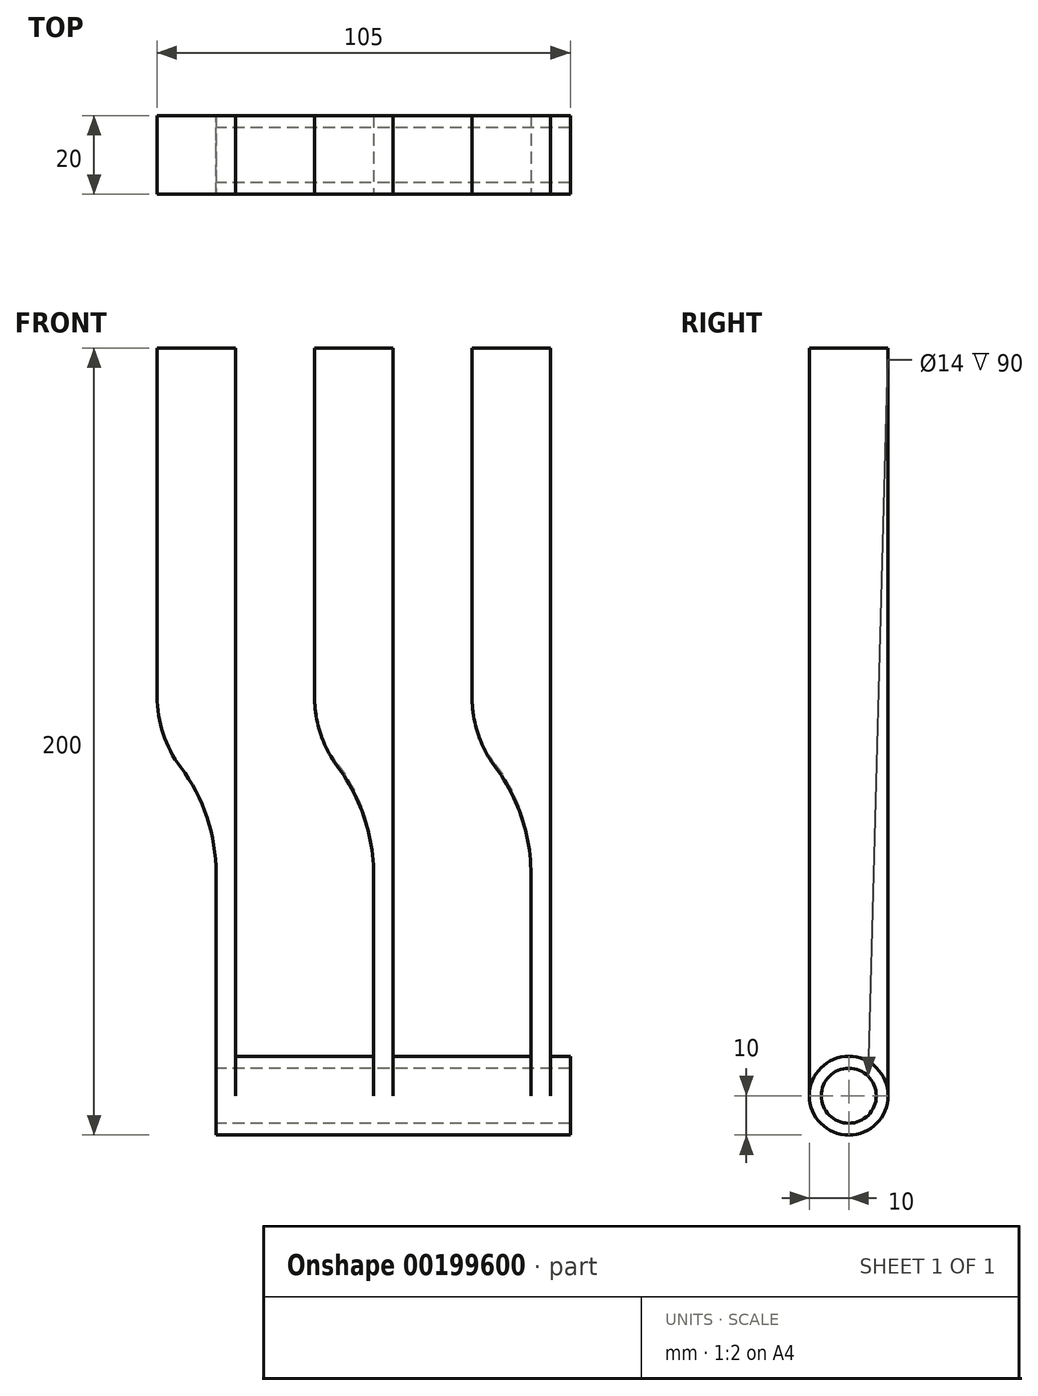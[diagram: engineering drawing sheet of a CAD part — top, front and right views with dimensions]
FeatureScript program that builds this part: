
annotation { "Feature Type Name" : "Feature", "Feature Type Description" : "" }
export const myFeature = defineFeature(function(context is Context, id is Id, definition is map)
    precondition{}
    {
        {
            assignVariable(context, id + "F0", {"name" : "width", "anyValue" : 120 * mm});
        }
        {
            var Q0;
            Q0=qCreatedBy(makeId("Front.planeOp"),FACE);
            var sketch = newSketch(context, id + "F1", { "sketchPlane" : qUnion([Q0])});
            skLineSegment(sketch, "E0.bottom", {"start": v(0, 0) * mm, "end": v(120, 0) * mm});
            skLineSegment(sketch, "E0.top", {"start": v(0, 200) * mm, "end": v(120, 200) * mm});
            skLineSegment(sketch, "E0.left", {"start": v(0, 0) * mm, "end": v(0, 200) * mm});
            skLineSegment(sketch, "E0.right", {"start": v(120, 0) * mm, "end": v(120, 200) * mm});
            skSolve(sketch);
        }
        {
            var Q0;
            Q0 = qSketchRegion(id + "F1", true);
            extrude(context, id + "F2", {"entities" : qUnion([Q0]), "depth" : 1 / 6 * getVariable(context, 'width')});
        }
        {
            var Q0;
            Q0=makeQuery(id+"F2.opExtrude","SWEPT_FACE",FACE,{"disambiguationData":[OSD([sQuery(id+"F1.wireOp",EDGE,"E0.left")])]});
            var sketch = newSketch(context, id + "F3", { "sketchPlane" : qUnion([Q0])});
            skCircle(sketch, "E1", {"center": v(10, 10) * mm, "radius": 10 * mm});
            skPoint(sketch, "E1.centerSnap0", {"position": v(10, 0) * mm});
            skSolve(sketch);
        }
        {
            var Q0;
            {var subQ0=sQuery(id+"F3.wireOp",EDGE,"E1");var subQ1=sQuery(id+"F1.wireOp",EDGE,"E0.left");var subQ2=makeQuery(id+"F2.opExtrude","CAP_EDGE",EDGE,{"disambiguationData":[OSD([subQ1])],"isStart":false});var subQ3=makeQuery(id+"F3.imprint","INTERSECT",VERTEX,{"derivedFrom":[subQ2,subQ0]});Q0=makeQuery(id+"F3.imprint","IMPRINT",FACE,{"disambiguationData":[TD([[makeQuery(id+"F3.imprint","IMPRINT",EDGE,{"disambiguationData":[TD([[subQ3,1.0]])],"derivedFrom":subQ0}),-1.0]])]});}
            var Q1;
            {var subQ0=sQuery(id+"F3.wireOp",EDGE,"E1");var subQ1=sQuery(id+"F1.wireOp",EDGE,"E0.left");var subQ2=makeQuery(id+"F2.opExtrude","CAP_EDGE",EDGE,{"disambiguationData":[OSD([subQ1])],"isStart":true});var subQ3=makeQuery(id+"F3.imprint","INTERSECT",VERTEX,{"derivedFrom":[subQ2,subQ0]});Q1=makeQuery(id+"F3.imprint","IMPRINT",FACE,{"disambiguationData":[TD([[makeQuery(id+"F3.imprint","IMPRINT",EDGE,{"disambiguationData":[TD([[subQ3,-1.0]])],"derivedFrom":subQ0}),-1.0]])]});}
            var Q2;
            Q2=makeQuery(id+"F2.opExtrude","CAP_EDGE",EDGE,{"disambiguationData":[OSD([sQuery(id+"F1.wireOp",EDGE,"E0.bottom")])],"isStart":false});
            sweep(context, id + "F4", {"operationType" : NewBodyOperationType.REMOVE, "profiles" : qUnion([Q0, Q1]), "path" : qUnion([Q2])});
        }
        {
            var Q0;
            Q0=makeQuery(id+"F2.opExtrude","CAP_FACE",FACE,{"disambiguationData":[OSD([sQuery(id+"F1.wireOp",EDGE,"E0.bottom"),sQuery(id+"F1.wireOp",EDGE,"E0.top"),sQuery(id+"F1.wireOp",EDGE,"E0.left"),sQuery(id+"F1.wireOp",EDGE,"E0.right")])],"isStart":false});
            var sketch = newSketch(context, id + "F5", { "sketchPlane" : qUnion([Q0])});
            skLineSegment(sketch, "E2", {"start": v(60, 200) * mm, "end": v(60, 10) * mm});
            skLineSegment(sketch, "E3", {"start": v(20, 200) * mm, "end": v(20, 10) * mm});
            skLineSegment(sketch, "E4", {"start": v(40, 200) * mm, "end": v(40, 10) * mm});
            skLineSegment(sketch, "E5.MirrorCS", {"start": v(80, 200) * mm, "end": v(80, 10) * mm});
            skLineSegment(sketch, "E6.MirrorCS", {"start": v(100, 200) * mm, "end": v(100, 10) * mm});
            skSolve(sketch);
        }
        {
            var Q0;
            {var subQ0=sQuery(id+"F5.wireOp",EDGE,"E3");Q0=makeQuery(id+"F5.imprint","IMPRINT",FACE,{"disambiguationData":[TD([[makeQuery(id+"F5.imprint","IMPRINT",EDGE,{"derivedFrom":subQ0}),1.0]])]});}
            var Q1;
            {var subQ0=sQuery(id+"F5.wireOp",EDGE,"E2");Q1=makeQuery(id+"F5.imprint","IMPRINT",FACE,{"disambiguationData":[TD([[makeQuery(id+"F5.imprint","IMPRINT",EDGE,{"derivedFrom":subQ0}),1.0]])]});}
            var Q2;
            {var subQ0=sQuery(id+"F5.wireOp",EDGE,"E6.MirrorCS");Q2=makeQuery(id+"F5.imprint","IMPRINT",FACE,{"disambiguationData":[TD([[makeQuery(id+"F5.imprint","IMPRINT",EDGE,{"derivedFrom":subQ0}),1.0]])]});}
            var Q3;
            Q3 = qConstructionFilter(qBodyType(qCreatedBy(id + "F3" ,EDGE), BodyType.WIRE), ConstructionObject.NO);
            sweep(context, id + "F6", {"operationType" : NewBodyOperationType.REMOVE, "profiles" : qUnion([Q0, Q1, Q2]), "path" : qUnion([Q3])});
        }
        {
            var Q0;
            Q0=makeQuery(id+"F2.opExtrude","SWEPT_FACE",FACE,{"disambiguationData":[OSD([sQuery(id+"F1.wireOp",EDGE,"E0.left")])]});
            var sketch = newSketch(context, id + "F7", { "sketchPlane" : qUnion([Q0])});
            skCircle(sketch, "E7", {"center": v(10, 10) * mm, "radius": 7 * mm});
            skSolve(sketch);
        }
        {
            var Q0;
            Q0 = qSketchRegion(id + "F7", true);
            extrude(context, id + "F8", {"entities" : qUnion([Q0]), "operationType" : NewBodyOperationType.REMOVE, "endBound" : BoundingType.THROUGH_ALL, "oppositeDirection" : true, "depth" : 25 * mm});
        }
        {
            var Q0;
            Q0=qCreatedBy(makeId("Front.planeOp"),FACE);
            var sketch = newSketch(context, id + "F9", { "sketchPlane" : qUnion([Q0])});
            skLineSegment(sketch, "E8.bottom", {"start": v(0, 100) * mm, "end": v(15, 100) * mm});
            skLineSegment(sketch, "E8.top", {"start": v(0, 0) * mm, "end": v(15, 0) * mm});
            skLineSegment(sketch, "E8.left", {"start": v(0, 100) * mm, "end": v(0, 0) * mm});
            skLineSegment(sketch, "E8.right", {"start": v(15, 100) * mm, "end": v(15, 0) * mm});
            skSolve(sketch);
        }
        {
            var Q0;
            Q0 = qSketchRegion(id + "F9", true);
            var Q1;
            Q1=makeQuery(id+"F2.opExtrude","SWEPT_EDGE",EDGE,{"disambiguationData":[OSD([sQuery(id+"F1.wireOp",EDGE,"E0.top"),sQuery(id+"F1.wireOp",EDGE,"E0.left")])]});
            sweep(context, id + "F10", {"operationType" : NewBodyOperationType.REMOVE, "profiles" : qUnion([Q0]), "path" : qUnion([Q1])});
        }
        {
            var Q0;
            Q0=qCreatedBy(makeId("Front.planeOp"),FACE);
            var sketch = newSketch(context, id + "F11", { "sketchPlane" : qUnion([Q0])});
            skLineSegment(sketch, "E9.bottom", {"start": v(40, 100) * mm, "end": v(55, 100) * mm});
            skLineSegment(sketch, "E9.top", {"start": v(40, 10) * mm, "end": v(55, 10) * mm});
            skLineSegment(sketch, "E9.left", {"start": v(40, 100) * mm, "end": v(40, 10) * mm});
            skLineSegment(sketch, "E9.right", {"start": v(55, 100) * mm, "end": v(55, 10) * mm});
            skLineSegment(sketch, "E10.bottom", {"start": v(80, 100) * mm, "end": v(95, 100) * mm});
            skLineSegment(sketch, "E10.top", {"start": v(80, 10) * mm, "end": v(95, 10) * mm});
            skLineSegment(sketch, "E10.left", {"start": v(80, 100) * mm, "end": v(80, 10) * mm});
            skLineSegment(sketch, "E10.right", {"start": v(95, 100) * mm, "end": v(95, 10) * mm});
            skSolve(sketch);
        }
        {
            var Q0;
            Q0 = qSketchRegion(id + "F11", true);
            var Q1;
            Q1=makeQuery(id+"F6.boolean.opBoolean","COPY",EDGE,{"derivedFrom":makeQuery(id+"F6.opSweep","SWEPT_EDGE",EDGE,{"disambiguationData":[OSD([sQuery(id+"F1.wireOp",EDGE,"E0.bottom"),sQuery(id+"F1.wireOp",EDGE,"E0.left"),sQuery(id+"F3.wireOp",EDGE,"E1"),sQuery(id+"F5.wireOp",EDGE,"E4")])]})});
            sweep(context, id + "F12", {"operationType" : NewBodyOperationType.REMOVE, "profiles" : qUnion([Q0]), "path" : qUnion([Q1])});
        }
        {
            var Q0;
            Q0=makeQuery(id+"F10.boolean.opBoolean","COPY",EDGE,{"derivedFrom":makeQuery(id+"F10.opSweep","SWEPT_EDGE",EDGE,{"disambiguationData":[OSD([sQuery(id+"F1.wireOp",EDGE,"E0.top"),sQuery(id+"F1.wireOp",EDGE,"E0.left"),sQuery(id+"F9.wireOp",EDGE,"E8.bottom"),sQuery(id+"F9.wireOp",EDGE,"E8.right")])]})});
            var Q1;
            Q1=makeQuery(id+"F12.boolean.opBoolean","COPY",EDGE,{"derivedFrom":makeQuery(id+"F12.opSweep","SWEPT_EDGE",EDGE,{"disambiguationData":[OSD([sQuery(id+"F1.wireOp",EDGE,"E0.bottom"),sQuery(id+"F1.wireOp",EDGE,"E0.left"),sQuery(id+"F3.wireOp",EDGE,"E1"),sQuery(id+"F5.wireOp",EDGE,"E4"),sQuery(id+"F11.wireOp",EDGE,"E9.bottom"),sQuery(id+"F11.wireOp",EDGE,"E9.right")])]})});
            var Q2;
            Q2=makeQuery(id+"F12.boolean.opBoolean","COPY",EDGE,{"derivedFrom":makeQuery(id+"F12.opSweep","SWEPT_EDGE",EDGE,{"disambiguationData":[OSD([sQuery(id+"F1.wireOp",EDGE,"E0.bottom"),sQuery(id+"F1.wireOp",EDGE,"E0.left"),sQuery(id+"F3.wireOp",EDGE,"E1"),sQuery(id+"F5.wireOp",EDGE,"E4"),sQuery(id+"F11.wireOp",EDGE,"E10.bottom"),sQuery(id+"F11.wireOp",EDGE,"E10.right")])]})});
            fillet(context, id + "F13", {"entities" : qUnion([Q0, Q1, Q2]), "radius" : 45 * mm, "tangentPropagation" : true, "allowEdgeOverflow" : false});
        }
        {
            var Q0;
            {var subQ0=sQuery(id+"F1.wireOp",EDGE,"E0.left");Q0=makeQuery(id+"F13.opFillet","BLEND_EDGE",EDGE,{"blendedFrom":[makeQuery(id+"F10.boolean.opBoolean","COPY",EDGE,{"derivedFrom":makeQuery(id+"F10.opSweep","SWEPT_EDGE",EDGE,{"disambiguationData":[OSD([sQuery(id+"F1.wireOp",EDGE,"E0.top"),subQ0,sQuery(id+"F9.wireOp",EDGE,"E8.bottom"),sQuery(id+"F9.wireOp",EDGE,"E8.right")])]})}),makeQuery(id+"F2.opExtrude","SWEPT_FACE",FACE,{"disambiguationData":[OSD([subQ0])]})],"blendedInto":[makeQuery(id+"F2.opExtrude","SWEPT_FACE",FACE,{"disambiguationData":[OSD([subQ0])]})]});}
            var Q1;
            {var subQ0=sQuery(id+"F5.wireOp",EDGE,"E4");var subQ1=sQuery(id+"F3.wireOp",EDGE,"E1");Q1=makeQuery(id+"F13.opFillet","BLEND_EDGE",EDGE,{"blendedFrom":[makeQuery(id+"F12.boolean.opBoolean","COPY",EDGE,{"derivedFrom":makeQuery(id+"F12.opSweep","SWEPT_EDGE",EDGE,{"disambiguationData":[OSD([sQuery(id+"F1.wireOp",EDGE,"E0.bottom"),sQuery(id+"F1.wireOp",EDGE,"E0.left"),subQ1,subQ0,sQuery(id+"F11.wireOp",EDGE,"E9.bottom"),sQuery(id+"F11.wireOp",EDGE,"E9.right")])]})}),makeQuery(id+"F6.boolean.opBoolean","COPY",FACE,{"derivedFrom":makeQuery(id+"F6.opSweep","SWEPT_FACE",FACE,{"disambiguationData":[OSD([subQ1,subQ0])]})})],"blendedInto":[makeQuery(id+"F6.boolean.opBoolean","COPY",FACE,{"derivedFrom":makeQuery(id+"F6.opSweep","SWEPT_FACE",FACE,{"disambiguationData":[OSD([subQ1,subQ0])]})})]});}
            var Q2;
            {var subQ0=sQuery(id+"F3.wireOp",EDGE,"E1");Q2=makeQuery(id+"F13.opFillet","BLEND_EDGE",EDGE,{"blendedFrom":[makeQuery(id+"F12.boolean.opBoolean","COPY",EDGE,{"derivedFrom":makeQuery(id+"F12.opSweep","SWEPT_EDGE",EDGE,{"disambiguationData":[OSD([sQuery(id+"F1.wireOp",EDGE,"E0.bottom"),sQuery(id+"F1.wireOp",EDGE,"E0.left"),subQ0,sQuery(id+"F5.wireOp",EDGE,"E4"),sQuery(id+"F11.wireOp",EDGE,"E10.bottom"),sQuery(id+"F11.wireOp",EDGE,"E10.right")])]})}),makeQuery(id+"F6.boolean.opBoolean","COPY",FACE,{"derivedFrom":makeQuery(id+"F6.opSweep","SWEPT_FACE",FACE,{"disambiguationData":[OSD([subQ0,sQuery(id+"F5.wireOp",EDGE,"E5.MirrorCS")])]})})],"blendedInto":[makeQuery(id+"F6.boolean.opBoolean","COPY",FACE,{"derivedFrom":makeQuery(id+"F6.opSweep","SWEPT_FACE",FACE,{"disambiguationData":[OSD([subQ0,sQuery(id+"F5.wireOp",EDGE,"E5.MirrorCS")])]})})]});}
            fillet(context, id + "F14", {"entities" : qUnion([Q0, Q1, Q2]), "radius" : 30 * mm, "tangentPropagation" : true, "allowEdgeOverflow" : false});
        }
        {
            var Q0;
            Q0=qCreatedBy(makeId("Front.planeOp"),FACE);
            var sketch = newSketch(context, id + "F15", { "sketchPlane" : qUnion([Q0])});
            skLineSegment(sketch, "E11.bottom", {"start": v(105, 0) * mm, "end": v(120, 0) * mm});
            skLineSegment(sketch, "E11.top", {"start": v(105, 20) * mm, "end": v(120, 20) * mm});
            skLineSegment(sketch, "E11.left", {"start": v(105, 0) * mm, "end": v(105, 20) * mm});
            skLineSegment(sketch, "E11.right", {"start": v(120, 0) * mm, "end": v(120, 20) * mm});
            skSolve(sketch);
        }
        {
            var Q0;
            Q0 = qSketchRegion(id + "F15", true);
            var Q1;
            Q1=makeQuery(id+"F6.boolean.opBoolean","INTERSECT",EDGE,{"derivedFrom":[makeQuery(id+"F2.opExtrude","SWEPT_FACE",FACE,{"disambiguationData":[OSD([sQuery(id+"F1.wireOp",EDGE,"E0.top")])]}),makeQuery(id+"F6.opSweep","SWEPT_FACE",FACE,{"disambiguationData":[OSD([sQuery(id+"F3.wireOp",EDGE,"E1"),sQuery(id+"F5.wireOp",EDGE,"E6.MirrorCS")])]})]});
            sweep(context, id + "F16", {"operationType" : NewBodyOperationType.REMOVE, "profiles" : qUnion([Q0]), "path" : qUnion([Q1])});
        }
    });
